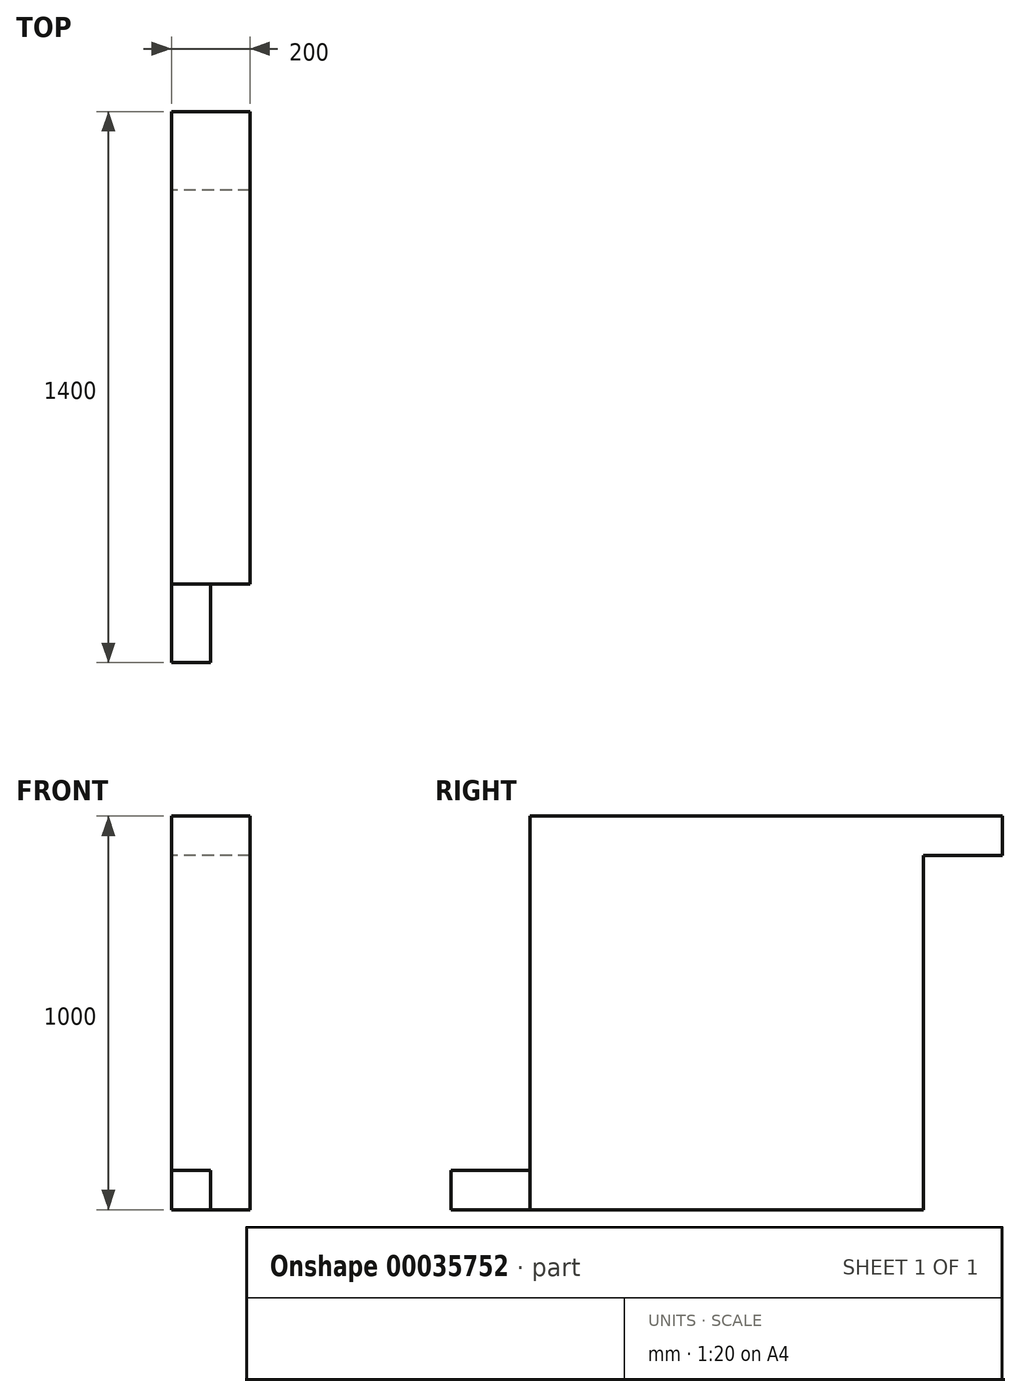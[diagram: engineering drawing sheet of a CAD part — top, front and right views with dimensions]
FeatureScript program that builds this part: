
annotation { "Feature Type Name" : "Feature", "Feature Type Description" : "" }
export const myFeature = defineFeature(function(context is Context, id is Id, definition is map)
    precondition{}
    {
        {
            var Q0;
            Q0=qCreatedBy(makeId("Top.planeOp"),FACE);
            var sketch = newSketch(context, id + "F0", { "sketchPlane" : qUnion([Q0])});
            skLineSegment(sketch, "E0.bottom", {"start": v(0, 0) * mm, "end": v(200, 0) * mm});
            skLineSegment(sketch, "E0.top", {"start": v(0, 1000) * mm, "end": v(200, 1000) * mm});
            skLineSegment(sketch, "E0.left", {"start": v(0, 0) * mm, "end": v(0, 1000) * mm});
            skLineSegment(sketch, "E0.right", {"start": v(200, 0) * mm, "end": v(200, 1000) * mm});
            skSolve(sketch);
        }
        {
            var Q0;
            Q0=makeQuery(id+"F0.imprint","IMPRINT",FACE,{"disambiguationData":[TD([[makeQuery(id+"F0.imprint","IMPRINT",EDGE,{"derivedFrom":sQuery(id+"F0.wireOp",EDGE,"E0.bottom")}),1.0]])]});
            extrude(context, id + "F1", {"entities" : qUnion([Q0]), "depth" : 1000 * mm});
        }
        {
            var Q0;
            Q0=makeQuery(id+"F1.opExtrude","SWEPT_FACE",FACE,{"disambiguationData":[OSD([sQuery(id+"F0.wireOp",EDGE,"E0.bottom")])]});
            var sketch = newSketch(context, id + "F2", { "sketchPlane" : qUnion([Q0])});
            skLineSegment(sketch, "E1.bottom", {"start": v(0, 0) * mm, "end": v(100, 0) * mm});
            skLineSegment(sketch, "E1.top", {"start": v(0, 100) * mm, "end": v(100, 100) * mm});
            skLineSegment(sketch, "E1.left", {"start": v(0, 0) * mm, "end": v(0, 100) * mm});
            skLineSegment(sketch, "E1.right", {"start": v(100, 0) * mm, "end": v(100, 100) * mm});
            skSolve(sketch);
        }
        {
            var Q0;
            Q0=makeQuery(id+"F2.imprint","IMPRINT",FACE,{"disambiguationData":[TD([[makeQuery(id+"F2.imprint","IMPRINT",EDGE,{"derivedFrom":sQuery(id+"F2.wireOp",EDGE,"E1.bottom")}),1.0]])]});
            extrude(context, id + "F3", {"entities" : qUnion([Q0]), "operationType" : NewBodyOperationType.ADD, "depth" : 200 * mm});
        }
        {
            var Q0;
            Q0=makeQuery(id+"F1.opExtrude","SWEPT_FACE",FACE,{"disambiguationData":[OSD([sQuery(id+"F0.wireOp",EDGE,"E0.top")])]});
            var sketch = newSketch(context, id + "F4", { "sketchPlane" : qUnion([Q0])});
            skLineSegment(sketch, "E2.bottom", {"start": v(-200, 1000) * mm, "end": v(0, 1000) * mm});
            skLineSegment(sketch, "E2.top", {"start": v(-200, 900) * mm, "end": v(0, 900) * mm});
            skLineSegment(sketch, "E2.left", {"start": v(-200, 1000) * mm, "end": v(-200, 900) * mm});
            skLineSegment(sketch, "E2.right", {"start": v(0, 1000) * mm, "end": v(0, 900) * mm});
            skSolve(sketch);
        }
        {
            var Q0;
            Q0=makeQuery(id+"F4.imprint","IMPRINT",FACE,{"disambiguationData":[TD([[makeQuery(id+"F4.imprint","IMPRINT",EDGE,{"derivedFrom":sQuery(id+"F4.wireOp",EDGE,"E2.bottom")}),1.0]])]});
            extrude(context, id + "F5", {"entities" : qUnion([Q0]), "operationType" : NewBodyOperationType.ADD, "depth" : 200 * mm});
        }
    });
